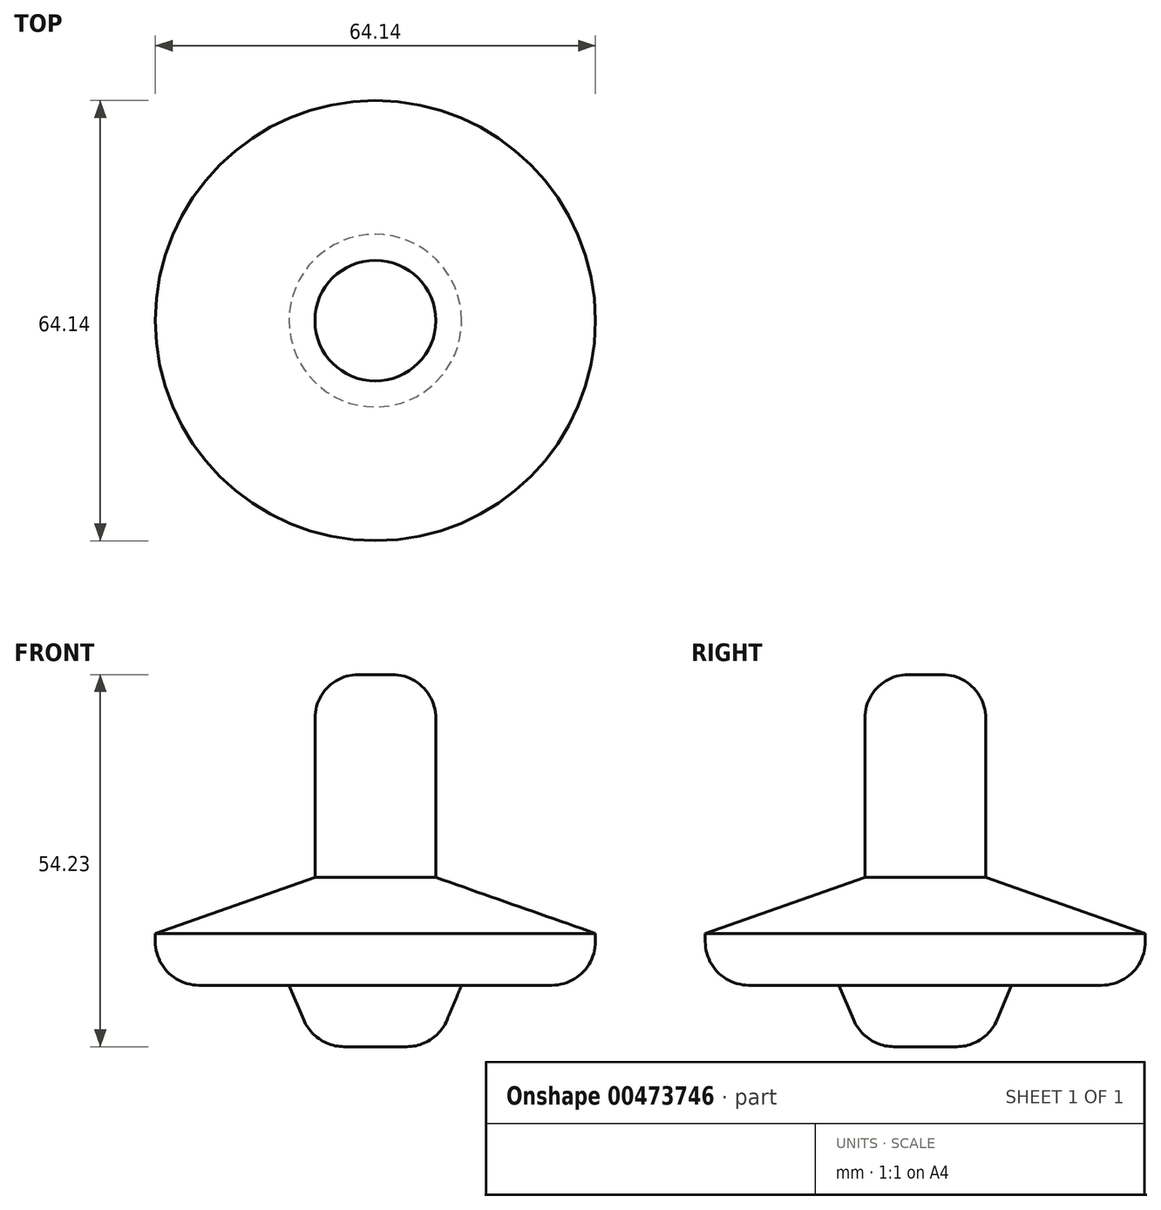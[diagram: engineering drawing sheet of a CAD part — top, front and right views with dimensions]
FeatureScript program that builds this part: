
annotation { "Feature Type Name" : "Feature", "Feature Type Description" : "" }
export const myFeature = defineFeature(function(context is Context, id is Id, definition is map)
    precondition{}
    {
        {
            var Q0;
            Q0=qCreatedBy(makeId("Front.planeOp"),FACE);
            var sketch = newSketch(context, id + "F0", { "sketchPlane" : qUnion([Q0])});
            skLineSegment(sketch, "E0", {"start": v(0, 0) * mm, "end": v(4.59, 0) * mm});
            skLineSegment(sketch, "E1", {"start": v(10.44, 3.89) * mm, "end": v(12.58, 8.96) * mm});
            skLineSegment(sketch, "E2", {"start": v(12.58, 8.96) * mm, "end": v(25.72, 8.96) * mm});
            skLineSegment(sketch, "E3", {"start": v(32.07, 15.3) * mm, "end": v(32.07, 16.5) * mm});
            skLineSegment(sketch, "E4", {"start": v(32.07, 16.5) * mm, "end": v(8.8, 24.68) * mm});
            skLineSegment(sketch, "E5", {"start": v(8.8, 24.68) * mm, "end": v(8.8, 47.88) * mm});
            skLineSegment(sketch, "E6", {"start": v(2.45, 54.23) * mm, "end": v(0, 54.23) * mm});
            skLineSegment(sketch, "E7", {"start": v(0, 54.23) * mm, "end": v(0, 0) * mm});
            skPoint(sketch, "E8.visualSharp", {"position": v(8.8, 0) * mm});
            skArc(sketch, "E8.filletArc", {"start": v(4.59, 0) * mm, "mid": v(8.1, 1.06) * mm, "end": v(10.44, 3.89) * mm});
            skPoint(sketch, "E9.visualSharp", {"position": v(32.07, 8.96) * mm});
            skArc(sketch, "E9.filletArc", {"start": v(25.72, 8.96) * mm, "mid": v(30.2, 10.82) * mm, "end": v(32.07, 15.3) * mm});
            skPoint(sketch, "E10.visualSharp", {"position": v(8.8, 54.23) * mm});
            skArc(sketch, "E10.filletArc", {"start": v(8.8, 47.88) * mm, "mid": v(6.94, 52.37) * mm, "end": v(2.45, 54.23) * mm});
            skSolve(sketch);
        }
        {
            var Q0;
            Q0 = qSketchRegion(id + "F0", true);
            var Q1;
            Q1=sQuery(id+"F0.wireOp",EDGE,"E7");
            revolve(context, id + "F1", {"entities" : qUnion([Q0]), "axis" : qUnion([Q1]), "revolveType" : RevolveType.FULL});
        }
    });
